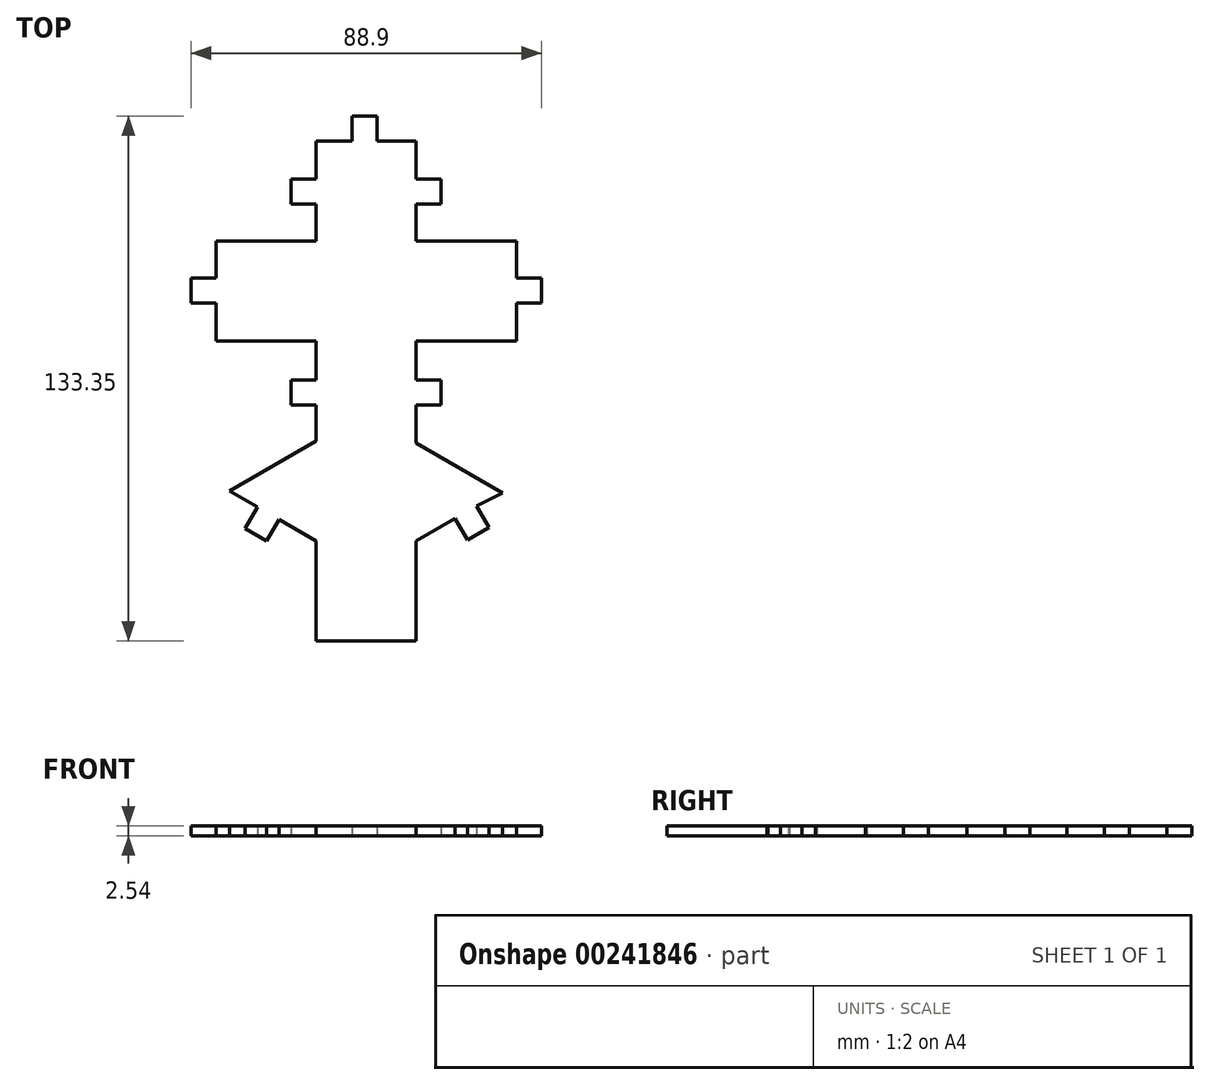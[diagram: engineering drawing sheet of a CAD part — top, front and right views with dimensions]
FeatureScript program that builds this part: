
annotation { "Feature Type Name" : "Feature", "Feature Type Description" : "" }
export const myFeature = defineFeature(function(context is Context, id is Id, definition is map)
    precondition{}
    {
        {
            var Q0;
            Q0=qCreatedBy(makeId("Top.planeOp"),FACE);
            var sketch = newSketch(context, id + "F0", { "sketchPlane" : qUnion([Q0])});
            skLineSegment(sketch, "E0.bottom", {"start": v(0, 34.05) * mm, "end": v(25.4, 34.05) * mm});
            skLineSegment(sketch, "E0.top", {"start": v(0, 8.65) * mm, "end": v(25.4, 8.65) * mm});
            skLineSegment(sketch, "E1.bottom", {"start": v(-25.4, 34.05) * mm, "end": v(-50.8, 34.05) * mm});
            skLineSegment(sketch, "E1.top", {"start": v(-25.4, 8.65) * mm, "end": v(-50.8, 8.65) * mm});
            skLineSegment(sketch, "E2", {"start": v(-25.4, -16.75) * mm, "end": v(-47.4, -29.45) * mm});
            skLineSegment(sketch, "E3", {"start": v(-0.06, -17.23) * mm, "end": v(21.94, -29.93) * mm});
            skLineSegment(sketch, "E4", {"start": v(-25.4, -67.55) * mm, "end": v(0, -67.55) * mm});
            skLineSegment(sketch, "E5", {"start": v(0, -42.15) * mm, "end": v(0, -67.55) * mm});
            skLineSegment(sketch, "E6", {"start": v(-25.4, -42.15) * mm, "end": v(-25.4, -67.55) * mm});
            skLineSegment(sketch, "E7", {"start": v(-40.3, -33.55) * mm, "end": v(-43.47, -39.05) * mm});
            skLineSegment(sketch, "E8", {"start": v(-43.47, -39.05) * mm, "end": v(-37.97, -42.22) * mm});
            skLineSegment(sketch, "E9", {"start": v(-37.97, -42.22) * mm, "end": v(-34.8, -36.72) * mm});
            skLineSegment(sketch, "E10", {"start": v(9.83, -36.47) * mm, "end": v(13, -41.97) * mm});
            skLineSegment(sketch, "E11", {"start": v(13, -41.97) * mm, "end": v(18.5, -38.8) * mm});
            skLineSegment(sketch, "E12", {"start": v(18.5, -38.8) * mm, "end": v(15.33, -33.3) * mm});
            skLineSegment(sketch, "E13", {"start": v(-50.8, 24.62) * mm, "end": v(-57.15, 24.62) * mm});
            skLineSegment(sketch, "E14", {"start": v(-57.15, 24.62) * mm, "end": v(-57.15, 18.27) * mm});
            skLineSegment(sketch, "E15", {"start": v(-57.15, 18.27) * mm, "end": v(-50.8, 18.27) * mm});
            skLineSegment(sketch, "E16", {"start": v(25.4, 24.62) * mm, "end": v(31.75, 24.62) * mm});
            skLineSegment(sketch, "E17", {"start": v(31.75, 24.62) * mm, "end": v(31.75, 18.27) * mm});
            skLineSegment(sketch, "E18", {"start": v(31.75, 18.27) * mm, "end": v(25.4, 18.27) * mm});
            skLineSegment(sketch, "E19", {"start": v(0, 49.82) * mm, "end": v(6.35, 49.82) * mm});
            skLineSegment(sketch, "E20", {"start": v(6.35, 49.82) * mm, "end": v(6.35, 43.47) * mm});
            skLineSegment(sketch, "E21", {"start": v(6.35, 43.47) * mm, "end": v(0, 43.47) * mm});
            skLineSegment(sketch, "E22", {"start": v(-25.4, 49.82) * mm, "end": v(-31.75, 49.82) * mm});
            skLineSegment(sketch, "E23", {"start": v(-31.75, 49.82) * mm, "end": v(-31.75, 43.47) * mm});
            skLineSegment(sketch, "E24", {"start": v(-31.75, 43.47) * mm, "end": v(-25.4, 43.47) * mm});
            skLineSegment(sketch, "E25", {"start": v(0, -1.21) * mm, "end": v(6.35, -1.21) * mm});
            skLineSegment(sketch, "E26", {"start": v(6.35, -1.21) * mm, "end": v(6.35, -7.56) * mm});
            skLineSegment(sketch, "E27", {"start": v(6.35, -7.56) * mm, "end": v(0, -7.56) * mm});
            skLineSegment(sketch, "E28", {"start": v(-25.4, -1.21) * mm, "end": v(-31.75, -1.21) * mm});
            skLineSegment(sketch, "E29", {"start": v(-31.75, -1.21) * mm, "end": v(-31.75, -7.56) * mm});
            skLineSegment(sketch, "E30", {"start": v(-31.75, -7.56) * mm, "end": v(-25.4, -7.56) * mm});
            skLineSegment(sketch, "E31", {"start": v(-16.38, 59.45) * mm, "end": v(-16.38, 65.8) * mm});
            skLineSegment(sketch, "E32", {"start": v(-16.38, 65.8) * mm, "end": v(-10.03, 65.8) * mm});
            skLineSegment(sketch, "E33", {"start": v(-10.03, 65.8) * mm, "end": v(-10.03, 59.45) * mm});
            skLineSegment(sketch, "E34", {"start": v(-50.8, 18.27) * mm, "end": v(-50.8, 8.65) * mm});
            skLineSegment(sketch, "E35", {"start": v(-50.8, 24.62) * mm, "end": v(-50.8, 34.05) * mm});
            skLineSegment(sketch, "E36", {"start": v(-25.4, 43.47) * mm, "end": v(-25.4, 34.05) * mm});
            skLineSegment(sketch, "E37", {"start": v(-25.4, 59.45) * mm, "end": v(-25.4, 49.82) * mm});
            skLineSegment(sketch, "E38", {"start": v(-16.38, 59.45) * mm, "end": v(-25.4, 59.45) * mm});
            skLineSegment(sketch, "E39", {"start": v(-10.03, 59.45) * mm, "end": v(0, 59.45) * mm});
            skLineSegment(sketch, "E40", {"start": v(0, 59.45) * mm, "end": v(0, 49.82) * mm});
            skLineSegment(sketch, "E41", {"start": v(0, 43.47) * mm, "end": v(0, 34.05) * mm});
            skLineSegment(sketch, "E42", {"start": v(25.4, 34.05) * mm, "end": v(25.4, 24.62) * mm});
            skLineSegment(sketch, "E43", {"start": v(25.4, 18.27) * mm, "end": v(25.4, 8.65) * mm});
            skLineSegment(sketch, "E44", {"start": v(0, -7.56) * mm, "end": v(-0.06, -17.23) * mm});
            skLineSegment(sketch, "E45", {"start": v(21.94, -29.93) * mm, "end": v(15.33, -33.3) * mm});
            skLineSegment(sketch, "E46", {"start": v(9.83, -36.47) * mm, "end": v(0, -42.15) * mm});
            skLineSegment(sketch, "E47", {"start": v(-34.8, -36.72) * mm, "end": v(-25.4, -42.15) * mm});
            skLineSegment(sketch, "E48", {"start": v(-47.4, -29.45) * mm, "end": v(-40.3, -33.55) * mm});
            skLineSegment(sketch, "E49", {"start": v(-25.4, 8.65) * mm, "end": v(-25.4, -1.21) * mm});
            skLineSegment(sketch, "E50", {"start": v(-25.4, -7.56) * mm, "end": v(-25.4, -16.75) * mm});
            skLineSegment(sketch, "E51", {"start": v(0, 8.65) * mm, "end": v(0, -1.21) * mm});
            skLineSegment(sketch, "E52", {"start": v(-25.4, 8.65) * mm, "end": v(-20.32, 8.65) * mm});
            skLineSegment(sketch, "E53", {"start": v(-25.4, 8.65) * mm, "end": v(-25.4, 13.73) * mm});
            skLineSegment(sketch, "E54", {"start": v(-25.4, 34.05) * mm, "end": v(-25.4, 28.97) * mm});
            skLineSegment(sketch, "E55", {"start": v(-25.4, 34.05) * mm, "end": v(-20.32, 34.05) * mm});
            skLineSegment(sketch, "E56", {"start": v(0, 34.05) * mm, "end": v(0, 28.97) * mm});
            skLineSegment(sketch, "E57", {"start": v(0, 34.05) * mm, "end": v(-5.08, 34.05) * mm});
            skLineSegment(sketch, "E58", {"start": v(0, 8.65) * mm, "end": v(0, 13.73) * mm});
            skLineSegment(sketch, "E59", {"start": v(0, 8.65) * mm, "end": v(-5.08, 8.65) * mm});
            skLineSegment(sketch, "E60", {"start": v(-25.4, -16.75) * mm, "end": v(-20.32, -16.75) * mm});
            skLineSegment(sketch, "E61", {"start": v(-25.4, -16.75) * mm, "end": v(-25.4, -21.83) * mm});
            skLineSegment(sketch, "E62", {"start": v(-25.4, -42.15) * mm, "end": v(-20.32, -42.15) * mm});
            skLineSegment(sketch, "E63", {"start": v(-25.4, -42.15) * mm, "end": v(-25.4, -37.07) * mm});
            skLineSegment(sketch, "E64", {"start": v(-0.06, -17.23) * mm, "end": v(-0.06, -22.3) * mm});
            skLineSegment(sketch, "E65", {"start": v(0, -37.07) * mm, "end": v(0, -42.15) * mm});
            skLineSegment(sketch, "E66", {"start": v(0, -42.15) * mm, "end": v(-5.08, -42.15) * mm});
            skLineSegment(sketch, "E67", {"start": v(-0.06, -17.23) * mm, "end": v(-5.33, -17.23) * mm});
            skSolve(sketch);
        }
        {
            var Q0;
            Q0 = qSketchRegion(id + "F0", true);
            var Q1;
            Q1=sQuery(id+"F0.wireOp",EDGE,"E1.bottom");
            var Q2;
            Q2=sQuery(id+"F0.wireOp",EDGE,"E35");
            var Q3;
            Q3=sQuery(id+"F0.wireOp",EDGE,"E13");
            var Q4;
            Q4=sQuery(id+"F0.wireOp",EDGE,"E14");
            var Q5;
            Q5=sQuery(id+"F0.wireOp",EDGE,"E15");
            var Q6;
            Q6=sQuery(id+"F0.wireOp",EDGE,"E34");
            var Q7;
            Q7=sQuery(id+"F0.wireOp",EDGE,"E1.top");
            var Q8;
            Q8=sQuery(id+"F0.wireOp",EDGE,"E49");
            var Q9;
            Q9=sQuery(id+"F0.wireOp",EDGE,"E28");
            var Q10;
            Q10=sQuery(id+"F0.wireOp",EDGE,"E29");
            var Q11;
            Q11=sQuery(id+"F0.wireOp",EDGE,"E30");
            var Q12;
            Q12=sQuery(id+"F0.wireOp",EDGE,"E50");
            var Q13;
            Q13=sQuery(id+"F0.wireOp",EDGE,"E2");
            var Q14;
            Q14=sQuery(id+"F0.wireOp",EDGE,"E48");
            var Q15;
            Q15=sQuery(id+"F0.wireOp",EDGE,"E7");
            var Q16;
            Q16=sQuery(id+"F0.wireOp",EDGE,"E8");
            var Q17;
            Q17=sQuery(id+"F0.wireOp",EDGE,"E9");
            var Q18;
            Q18=sQuery(id+"F0.wireOp",EDGE,"E47");
            var Q19;
            Q19=sQuery(id+"F0.wireOp",EDGE,"E6");
            var Q20;
            Q20=sQuery(id+"F0.wireOp",EDGE,"E4");
            var Q21;
            Q21=sQuery(id+"F0.wireOp",EDGE,"E5");
            var Q22;
            Q22=sQuery(id+"F0.wireOp",EDGE,"E46");
            var Q23;
            Q23=sQuery(id+"F0.wireOp",EDGE,"E10");
            var Q24;
            Q24=sQuery(id+"F0.wireOp",EDGE,"E11");
            var Q25;
            Q25=sQuery(id+"F0.wireOp",EDGE,"E12");
            var Q26;
            Q26=sQuery(id+"F0.wireOp",EDGE,"E45");
            var Q27;
            Q27=sQuery(id+"F0.wireOp",EDGE,"E3");
            var Q28;
            Q28=sQuery(id+"F0.wireOp",EDGE,"E44");
            var Q29;
            Q29=sQuery(id+"F0.wireOp",EDGE,"E27");
            var Q30;
            Q30=sQuery(id+"F0.wireOp",EDGE,"E26");
            var Q31;
            Q31=sQuery(id+"F0.wireOp",EDGE,"E25");
            var Q32;
            Q32=sQuery(id+"F0.wireOp",EDGE,"zN1MjhKy-DtAP-oZZu-bHx1-QPWTEEDiOYRn");
            var Q33;
            Q33=sQuery(id+"F0.wireOp",EDGE,"E0.top");
            var Q34;
            Q34=sQuery(id+"F0.wireOp",EDGE,"E43");
            var Q35;
            Q35=sQuery(id+"F0.wireOp",EDGE,"E18");
            var Q36;
            Q36=sQuery(id+"F0.wireOp",EDGE,"E17");
            var Q37;
            Q37=sQuery(id+"F0.wireOp",EDGE,"E16");
            var Q38;
            Q38=sQuery(id+"F0.wireOp",EDGE,"E42");
            var Q39;
            Q39=sQuery(id+"F0.wireOp",EDGE,"E0.bottom");
            var Q40;
            Q40=sQuery(id+"F0.wireOp",EDGE,"E41");
            var Q41;
            Q41=sQuery(id+"F0.wireOp",EDGE,"E36");
            var Q42;
            Q42=sQuery(id+"F0.wireOp",EDGE,"E21");
            var Q43;
            Q43=sQuery(id+"F0.wireOp",EDGE,"E20");
            var Q44;
            Q44=sQuery(id+"F0.wireOp",EDGE,"E19");
            var Q45;
            Q45=sQuery(id+"F0.wireOp",EDGE,"E40");
            var Q46;
            Q46=sQuery(id+"F0.wireOp",EDGE,"E39");
            var Q47;
            Q47=sQuery(id+"F0.wireOp",EDGE,"E33");
            var Q48;
            Q48=sQuery(id+"F0.wireOp",EDGE,"E32");
            var Q49;
            Q49=sQuery(id+"F0.wireOp",EDGE,"E31");
            var Q50;
            Q50=sQuery(id+"F0.wireOp",EDGE,"E38");
            var Q51;
            Q51=sQuery(id+"F0.wireOp",EDGE,"E37");
            var Q52;
            Q52=sQuery(id+"F0.wireOp",EDGE,"E22");
            var Q53;
            Q53=sQuery(id+"F0.wireOp",EDGE,"E23");
            var Q54;
            Q54=sQuery(id+"F0.wireOp",EDGE,"E24");
            extrude(context, id + "F1", {"entities" : qUnion([Q0]), "surfaceEntities" : qUnion([Q1, Q2, Q3, Q4, Q5, Q6, Q7, Q8, Q9, Q10, Q11, Q12, Q13, Q14, Q15, Q16, Q17, Q18, Q19, Q20, Q21, Q22, Q23, Q24, Q25, Q26, Q27, Q28, Q29, Q30, Q31, Q32, Q33, Q34, Q35, Q36, Q37, Q38, Q39, Q40, Q41, Q42, Q43, Q44, Q45, Q46, Q47, Q48, Q49, Q50, Q51, Q52, Q53, Q54]), "depth" : 2.54 * mm});
        }
    });
